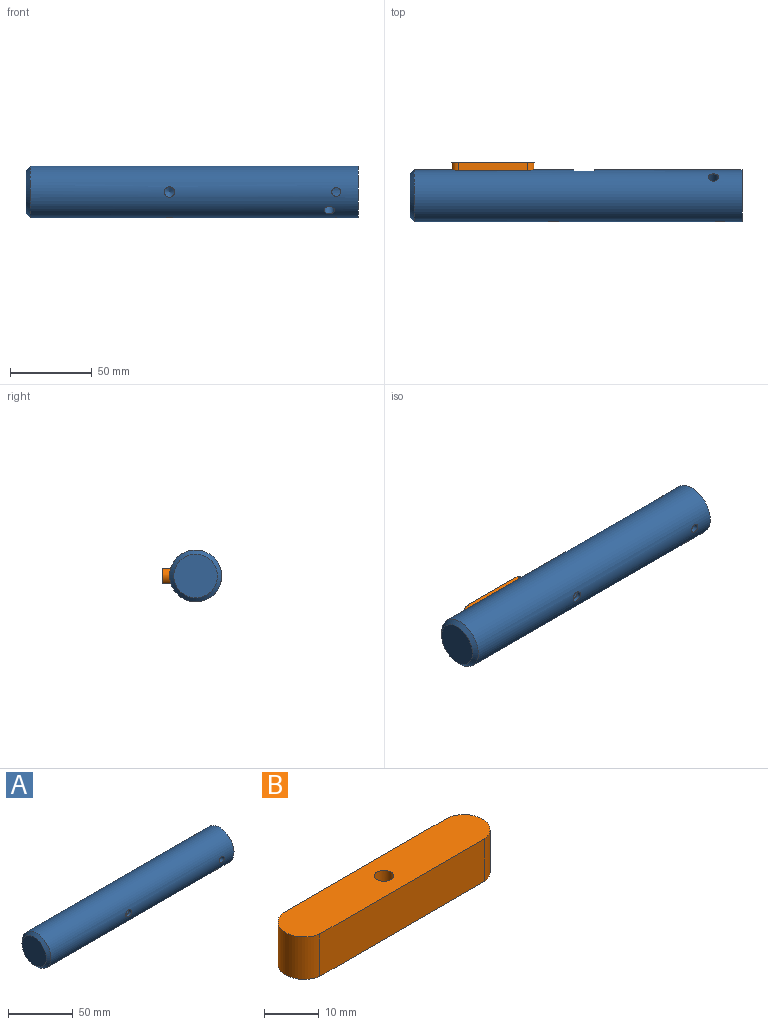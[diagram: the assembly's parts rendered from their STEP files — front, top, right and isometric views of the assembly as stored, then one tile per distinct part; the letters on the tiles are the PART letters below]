
ASSEMBLY  parts=2 mates=1
PART A: 64 faces, bbox 203.2x31.8x31.8 mm
  f0: cylinder r=15.88mm len=200.66mm, axis (-1,0,0), area 19227.2mm2, adj f2,f3,f5,f6,f7,f8,f11,f12
  f1: cylinder r=9.53mm len=25.4mm, axis (1,0,0), area 1409.6mm2, adj f3,f10,f54,f55,f60,f61
  f2: plane 12.7x11.18mm, normal (0,1,0), area 105.7mm2, adj f0,f11,f12,f13,f14,f15,f16,f17
  f3: plane 31.75x31.75mm, normal (1,0,0), area 506.7mm2, adj f0,f1
  f4: plane 26.67x26.67mm, normal (-1,0,0), area 558.6mm2, adj f53
  f5: plane 42.57x4.36mm, normal (0,0,-1), area 185.5mm2, adj f0,f6,f8,f9
  f6: cylinder r=4.78mm len=9.47mm, axis (0,1,0), area 65mm2, adj f0,f5,f7,f9
  f7: plane 42.57x4.36mm, normal (0,0,1), area 185.5mm2, adj f0,f6,f8,f9
  f8: cylinder r=4.78mm len=9.47mm, axis (0,1,0), area 65mm2, adj f0,f5,f7,f9
  f9: plane 50.8x9.47mm, normal (0,1,0), area 453.1mm2, adj f5,f6,f7,f8,f63
  f10: plane 19.05x19.05mm, normal (1,0,0), area 285mm2, adj f1
  f11: plane 11.18x1.02mm, normal (-1,0,0), area 7.6mm2, adj f0,f2
  f12: plane 11.18x1.02mm, normal (1,0,0), area 7.6mm2, adj f0,f2
  f13: plane 0.92x0.25mm, normal (0,0,1), area 0.2mm2, adj f2,f14,f32,f33
  f14: extruded ~2.14x0.36mm, area 0.6mm2, adj f2,f13,f15,f33
  f15: extruded ~2.03x0.57mm, area 0.5mm2, adj f2,f14,f16,f33
  f16: extruded ~1.56x0.72mm, area 0.5mm2, adj f2,f15,f17,f33
  f17: extruded ~1.24x0.43mm, area 0.3mm2, adj f2,f16,f18,f33
  f18: extruded ~1.7x0.94mm, area 0.5mm2, adj f2,f17,f19,f33
  f19: extruded ~1.4x0.69mm, area 0.4mm2, adj f2,f18,f20,f33
  f20: extruded ~0.85x0.34mm, area 0.2mm2, adj f2,f19,f21,f33
  f21: extruded ~1.51x1.08mm, area 0.5mm2, adj f2,f20,f22,f33
  f22: extruded ~1.86x0.4mm, area 0.5mm2, adj f2,f21,f23,f33
  f23: plane 0.85x0.33mm, normal (0.36,0,-0.93), area 0.2mm2, adj f2,f22,f24,f33
  f24: extruded ~2.15x0.4mm, area 0.6mm2, adj f2,f23,f25,f33
  f25: extruded ~1.82x0.51mm, area 0.5mm2, adj f2,f24,f26,f33
  f26: extruded ~1.41x0.66mm, area 0.4mm2, adj f2,f25,f27,f33
  f27: extruded ~1.36x0.47mm, area 0.4mm2, adj f2,f26,f28,f33
  f28: extruded ~1.54x0.9mm, area 0.5mm2, adj f2,f27,f29,f33
  f29: extruded ~1.48x0.69mm, area 0.4mm2, adj f2,f28,f30,f33
  f30: extruded ~0.83x0.36mm, area 0.2mm2, adj f2,f29,f31,f33
  f31: extruded ~1.81x1.24mm, area 0.6mm2, adj f2,f30,f32,f33
  f32: extruded ~2.14x0.44mm, area 0.6mm2, adj f2,f13,f31,f33
  f33: plane 7.77x4.89mm, normal (0,1,0), area 14.4mm2, adj f13,f14,f15,f16,f17,f18,f19,f20
  f34: plane 0.8x0.25mm, normal (1,0,0), area 0.2mm2, adj f2,f35,f51,f52
  f35: plane 6.61x1.44mm, normal (0.21,0,-0.98), area 1.7mm2, adj f2,f34,f36,f52
  f36: plane 0.25x0.04mm, normal (1,0,0), area 0mm2, adj f2,f35,f37,f52
  f37: extruded ~2.1x0.25mm, area 0.5mm2, adj f2,f36,f38,f52
  f38: plane 4.52x0.25mm, normal (0,0,1), area 1.1mm2, adj f2,f37,f39,f52
  f39: plane 0.78x0.25mm, normal (1,0,0), area 0.2mm2, adj f2,f38,f40,f52
  f40: plane 7.56x0.25mm, normal (0,0,-1), area 1.9mm2, adj f2,f39,f41,f52
  f41: plane 1.28x0.25mm, normal (-1,0,0), area 0.3mm2, adj f2,f40,f42,f52
  f42: plane 6.16x1.28mm, normal (-0.2,0,0.98), area 1.6mm2, adj f2,f41,f43,f52
  f43: plane 0.25x0.03mm, normal (-1,0,0), area 0mm2, adj f2,f42,f44,f52
  f44: plane 6.16x1.29mm, normal (-0.21,0,-0.98), area 1.6mm2, adj f2,f43,f45,f52
  f45: plane 1.3x0.25mm, normal (-1,0,0), area 0.3mm2, adj f2,f44,f46,f52
  f46: plane 7.56x0.25mm, normal (0,0,1), area 1.9mm2, adj f2,f45,f47,f52
  f47: plane 0.79x0.25mm, normal (1,0,0), area 0.2mm2, adj f2,f46,f48,f52
  f48: plane 4.58x0.25mm, normal (0,0,-1), area 1.2mm2, adj f2,f47,f49,f52
  f49: extruded ~2.02x0.25mm, area 0.5mm2, adj f2,f48,f50,f52
  f50: plane 0.25x0.04mm, normal (1,0,0), area 0mm2, adj f2,f49,f51,f52
  f51: plane 6.6x1.46mm, normal (0.22,0,0.98), area 1.7mm2, adj f2,f34,f50,f52
  f52: plane 7.56x5.18mm, normal (0,1,0), area 21.9mm2, adj f34,f35,f36,f37,f38,f39,f40,f41
  f53: cone r=15.88mm half-angle=45deg, axis (1,0,0), area 329.6mm2, adj f0,f4
  f54: cylinder r=2.71mm len=6.74mm, axis (0,-1,0), area 109.3mm2, adj f0,f1
  f55: cylinder r=2.71mm len=6.74mm, axis (0,0,-1), area 109.3mm2, adj f0,f1
  f56: cylinder r=3.17mm len=6.35mm, axis (0,0,-1), area 53.9mm2, adj f0,f57
  f57: cone r=0mm half-angle=59deg, axis (0,0,-1), area 36.9mm2, adj f56
  f58: cylinder r=3.17mm len=6.35mm, axis (0,-1,0), area 53.9mm2, adj f0,f59
  f59: cone r=0mm half-angle=59deg, axis (0,-1,0), area 36.9mm2, adj f58
  f60: cylinder r=3.17mm len=9.37mm, axis (0,-0.71,-0.71), area 128.9mm2, adj f0,f1
  f61: cylinder r=3.17mm len=9.37mm, axis (0,-0.71,-0.71), area 128.9mm2, adj f0,f1
  f62: cone r=0mm half-angle=59deg, axis (0,1,0), area 10.9mm2, adj f63
  f63: cylinder r=1.73mm len=11.15mm, axis (0,1,0), area 121mm2, adj f9,f62
PART B: 9 faces, bbox 50.8x9.5x9.5 mm
  f0: plane 42.57x9.49mm, normal (0,1,0), area 403.8mm2, adj f1,f3,f4,f5
  f1: cylinder r=4.78mm len=9.49mm, axis (0,0,-1), area 129.9mm2, adj f0,f2,f4,f5
  f2: plane 42.57x9.49mm, normal (0,-1,0), area 403.8mm2, adj f1,f3,f4,f5
  f3: cylinder r=4.78mm len=9.49mm, axis (0,0,-1), area 129.9mm2, adj f0,f2,f4,f5
  f4: plane 50.8x9.47mm, normal (0,0,1), area 453.1mm2, adj f0,f1,f2,f3,f6
  f5: plane 50.8x9.47mm, normal (0,0,-1), area 413mm2, adj f0,f1,f2,f3,f8
  f6: cylinder r=1.73mm len=5.32mm, axis (0,0,-1), area 57.7mm2, adj f4,f7
  f7: plane 7.94x7.94mm, normal (0,0,-1), area 40.1mm2, adj f6,f8
  f8: cylinder r=3.97mm len=7.94mm, axis (0,0,-1), area 103.9mm2, adj f5,f7
PLACE A t=(36.72,-6.33,-27.18)mm
PLACE B rot(axis=(1,0,0),90deg) t=(87.52,13.95,-27.18)mm
MATE fastened B.f1 <-> A.f6  axis (0,-1,0) through (66.9,4.46,-27.18)mm
